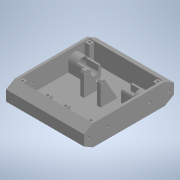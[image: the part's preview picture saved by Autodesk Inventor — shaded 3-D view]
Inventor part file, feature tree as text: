
AUTODESK INVENTOR PART (.ipt)
format: ipt  version: 2020 (Build 240168000, 168)  size: 380,416 bytes
history: native  units: in
note: dims shown in document units (in); Inventor stores cm internally (conversion verified against a paired STEP export)
features: projected_geometry x13, extrude x11, sketch x11, mirror x4, plane x1
ambient origin geometry x8: Origin, YZ Plane, XZ Plane, XY Plane, X Axis, Y Axis, Z Axis, Center Point
bodies: Solid1 (feature_tree)
feature tree (40):
  extrude  "Extrusion1"  Depth=5.9055in
  extrude  "Extrusion2"  TaperAngle=0.0deg  [1 undecoded]
  extrude  "Extrusion3"  Depth=1.2598in
  extrude  "Extrusion4"  Depth=0.315in
  extrude  "Extrusion5"  TaperAngle=0.0deg  [1 undecoded]
  extrude  "Extrusion6"  Depth=0.689in
  mirror  "Mirror1"
  extrude  "Extrusion7"  Depth=0.0787in
  mirror  "Mirror2"
  extrude  "Extrusion8"  Depth=0.5512in
  mirror  "Mirror3"
  plane  "Work Plane1"
  extrude  "Extrusion9"  Depth=0.7874in TaperAngle=0.0deg
  mirror  "Mirror4"
  extrude  "Extrusion10"  Depth=6.063in TaperAngle=0.0deg
  extrude  "Extrusion11"  Depth=0.1575in
  sketch  "Sketch1"  dims[d0=1.378in d1=5.9055in]
  sketch  "Sketch2"  dims[d2=5.1181in d3=0.0in]
  projected_geometry  "Projected Loop1"
  sketch  "Sketch3"  dims[d4=0.1575in d5=1.2598in]
  projected_geometry  "Projected Loop2"
  projected_geometry  "Projected Loop3"
  sketch  "Sketch4"  dims[d6=0.0in d8=0.315in]
  sketch  "Sketch5"  dims[d10=1.1898in d11=0.0in]
  projected_geometry  "Projected Loop4"
  sketch  "Sketch6"  dims[d12=0.6496in d13=0.689in]
  sketch  "Sketch7"  dims[d14=1.5748in d15=0.0787in]
  sketch  "Sketch9"  dims[d16=0.5512in d17=0.0in d18=0.6102in]
  sketch  "Sketch10"  dims[d19=0.4803in d20=0.7874in d21=0.0in]
  sketch  "Sketch12"  dims[d22=0.1654in d23=6.063in d24=0.0in]
  projected_geometry  "Projected Loop6"
  projected_geometry  "Projected Loop7"
  projected_geometry  "Projected Loop8"
  sketch  "Sketch13"  dims[d25=0.5967in d26=0.1575in d27=1.5748in d28=0.0in d29=0.0in d30=0.1575in d31=0.2756in d32=0.0in d33=0.4331in d34=0.122in d38=2.7559in d40=0.061in d41=0.0909in d42=0.2362in d43=0.0in d44=60.0deg d45=0.0787in d46=0.315in d48=1.1898in d49=0.0in d51=0.1575in d52=0.1575in d53=0.2756in d54=0.0in]
  projected_geometry  "Projected Loop9"
  projected_geometry  "Projected Loop10"
  projected_geometry  "Projected Loop11"
  projected_geometry  "Projected Loop12"
  projected_geometry  "Projected Loop13"
  projected_geometry  "Projected Loop14"
note: 2 required parameter values undecoded (feature->parameter linkage not recoverable at this tier; creation-order binding heuristic only, values carry confidence <= 0.55)
